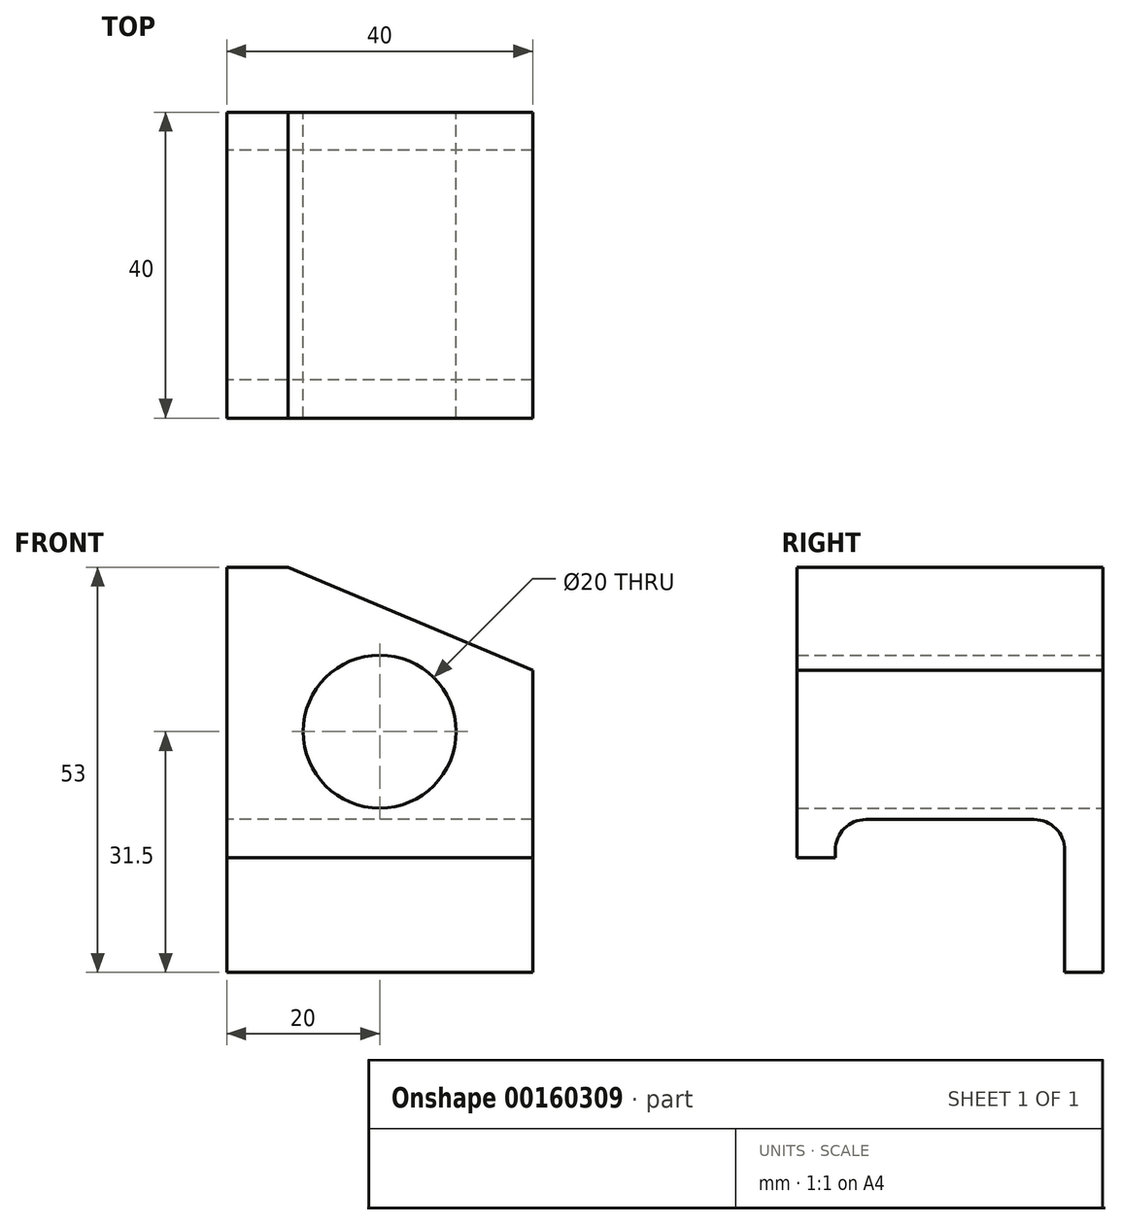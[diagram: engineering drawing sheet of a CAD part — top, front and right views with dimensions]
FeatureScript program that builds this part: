
annotation { "Feature Type Name" : "Feature", "Feature Type Description" : "" }
export const myFeature = defineFeature(function(context is Context, id is Id, definition is map)
    precondition{}
    {
        {
            var Q0;
            Q0=qCreatedBy(makeId("Front.planeOp"),FACE);
            var sketch = newSketch(context, id + "F0", { "sketchPlane" : qUnion([Q0])});
            skLineSegment(sketch, "E0.bottom", {"start": v(-20, 21.5) * mm, "end": v(-12, 21.5) * mm});
            skLineSegment(sketch, "E0.top", {"start": v(-20, -21.5) * mm, "end": v(20, -21.5) * mm});
            skLineSegment(sketch, "E0.left", {"start": v(-20, 21.5) * mm, "end": v(-20, -21.5) * mm});
            skLineSegment(sketch, "E0.right", {"start": v(20, 8) * mm, "end": v(20, -21.5) * mm});
            skPoint(sketch, "E0.middle", {"position": v(0, 0) * mm});
            skCircle(sketch, "E1", {"center": v(0, 0) * mm, "radius": 14 * mm, "construction": true});
            skCircle(sketch, "E2", {"center": v(0, 0) * mm, "radius": 10 * mm});
            skLineSegment(sketch, "E3", {"start": v(-12, 21.5) * mm, "end": v(20, 8) * mm});
            skPoint(sketch, "E4.orphan", {"position": v(20, 21.5) * mm});
            skSolve(sketch);
        }
        {
            var Q0;
            Q0=makeQuery(id+"F0.imprint","IMPRINT",FACE,{"disambiguationData":[TD([[makeQuery(id+"F0.imprint","IMPRINT",EDGE,{"derivedFrom":sQuery(id+"F0.wireOp",EDGE,"E0.bottom")}),-1.0]])]});
            extrude(context, id + "F1", {"entities" : qUnion([Q0]), "endBound" : BoundingType.SYMMETRIC, "depth" : 40 * mm});
        }
        {
            var Q0;
            Q0=makeQuery(id+"F1.opExtrude","SWEPT_FACE",FACE,{"disambiguationData":[OSD([sQuery(id+"F0.wireOp",EDGE,"E0.top")])]});
            extrude(context, id + "F2", {"entities" : qUnion([Q0]), "operationType" : NewBodyOperationType.ADD, "depth" : 10 * mm});
        }
        {
            var Q0;
            {var subQ0=sQuery(id+"F0.wireOp",EDGE,"E0.left");Q0=makeQuery(id+"F2.boolean.opBoolean","MERGE",FACE,{"derivedFrom":[makeQuery(id+"F1.opExtrude","SWEPT_FACE",FACE,{"disambiguationData":[OSD([subQ0])]}),makeQuery(id+"F2.opExtrude","SWEPT_FACE",FACE,{"disambiguationData":[OSD([sQuery(id+"F0.wireOp",EDGE,"E0.top"),subQ0])]})]});}
            var sketch = newSketch(context, id + "F3", { "sketchPlane" : qUnion([Q0])});
            skLineSegment(sketch, "E5", {"start": v(-15, -31.5) * mm, "end": v(-15, -11.5) * mm});
            skLineSegment(sketch, "E6", {"start": v(-15, -11.5) * mm, "end": v(15, -11.5) * mm});
            skLineSegment(sketch, "E7", {"start": v(15, -11.5) * mm, "end": v(15, -16.5) * mm});
            skLineSegment(sketch, "E8", {"start": v(15, -16.5) * mm, "end": v(20, -16.5) * mm});
            skLineSegment(sketch, "E9", {"start": v(20, -16.5) * mm, "end": v(20, -31.5) * mm});
            skLineSegment(sketch, "E10", {"start": v(20, -31.5) * mm, "end": v(-15, -31.5) * mm});
            skSolve(sketch);
        }
        {
            var Q0;
            Q0=makeQuery(id+"F3.imprint","IMPRINT",FACE,{"disambiguationData":[TD([[makeQuery(id+"F3.imprint","IMPRINT",EDGE,{"derivedFrom":sQuery(id+"F3.wireOp",EDGE,"E5")}),-1.0]])]});
            extrude(context, id + "F4", {"entities" : qUnion([Q0]), "operationType" : NewBodyOperationType.REMOVE, "endBound" : BoundingType.THROUGH_ALL, "oppositeDirection" : true, "depth" : 25 * mm});
        }
        {
            var Q0;
            {var subQ0=sQuery(id+"F3.wireOp",EDGE,"E5");var subQ1=sQuery(id+"F0.wireOp",EDGE,"E0.left");var subQ2=sQuery(id+"F3.wireOp",EDGE,"E6");Q0=makeQuery(id+"F4.boolean.opBoolean","COPY",EDGE,{"disambiguationData":[TD([makeQuery(id+"F1.opExtrude","SWEPT_FACE",FACE,{"disambiguationData":[OSD([subQ1])]})])],"derivedFrom":makeQuery(id+"F4.opExtrude","SWEPT_EDGE",EDGE,{"disambiguationData":[OSD([subQ0,subQ2])]})});}
            var Q1;
            {var subQ0=sQuery(id+"F3.wireOp",EDGE,"E6");var subQ1=sQuery(id+"F0.wireOp",EDGE,"E0.left");var subQ2=sQuery(id+"F3.wireOp",EDGE,"E7");Q1=makeQuery(id+"F4.boolean.opBoolean","COPY",EDGE,{"disambiguationData":[TD([makeQuery(id+"F1.opExtrude","SWEPT_FACE",FACE,{"disambiguationData":[OSD([subQ1])]})])],"derivedFrom":makeQuery(id+"F4.opExtrude","SWEPT_EDGE",EDGE,{"disambiguationData":[OSD([subQ0,subQ2])]})});}
            fillet(context, id + "F5", {"entities" : qUnion([Q0, Q1]), "radius" : 4 * mm, "tangentPropagation" : true, "allowEdgeOverflow" : false});
        }
    });
